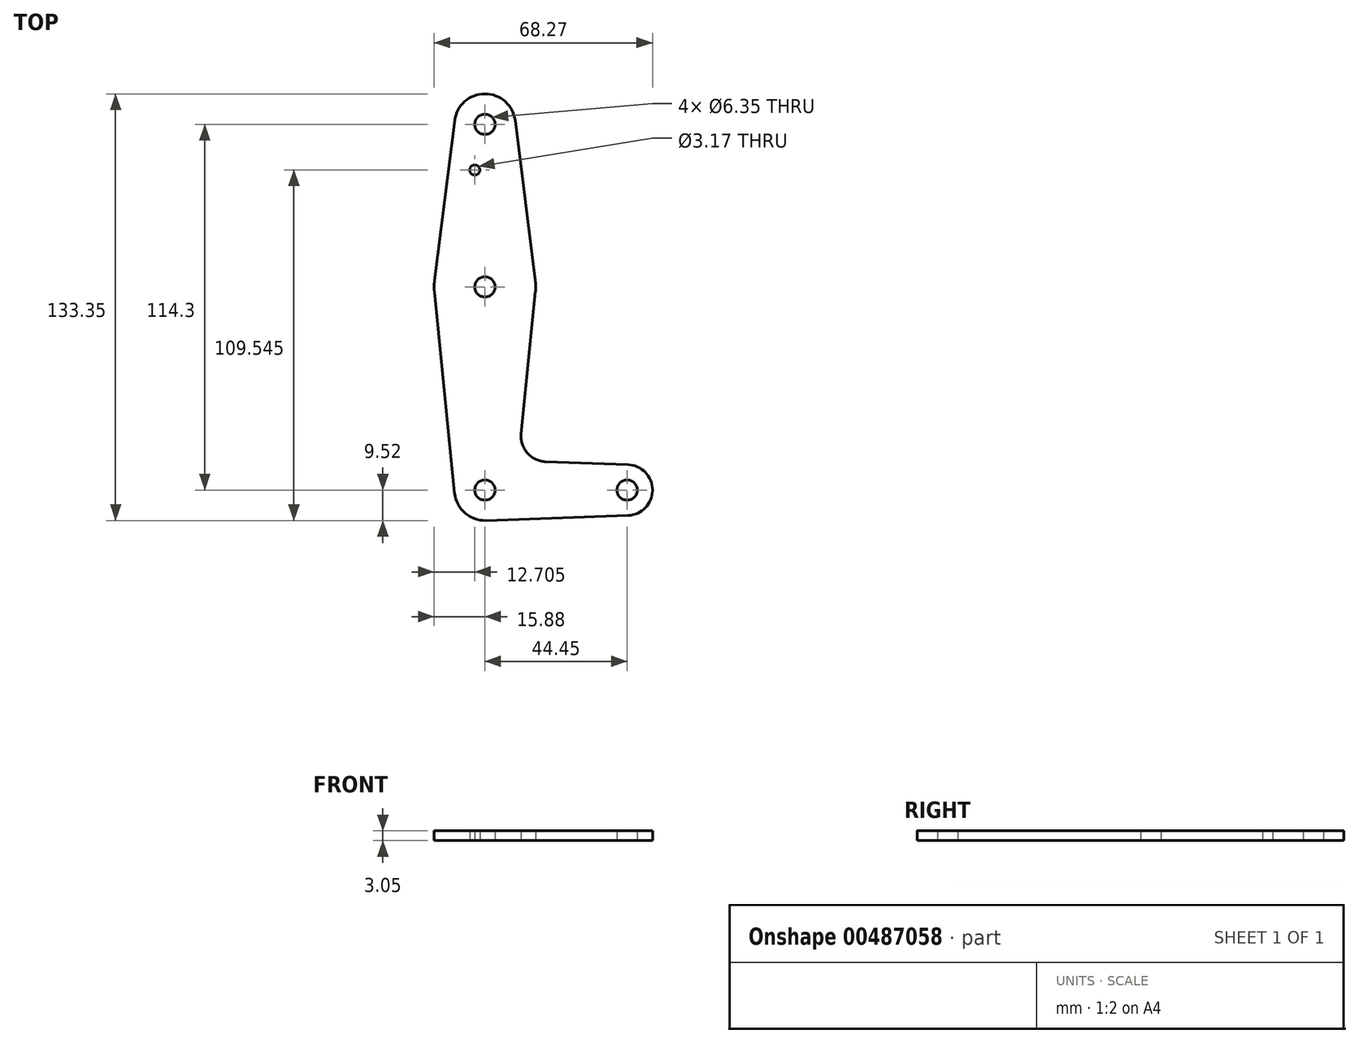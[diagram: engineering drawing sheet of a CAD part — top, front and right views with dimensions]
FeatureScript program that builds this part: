
annotation { "Feature Type Name" : "Feature", "Feature Type Description" : "" }
export const myFeature = defineFeature(function(context is Context, id is Id, definition is map)
    precondition{}
    {
        {
            var Q0;
            Q0=qCreatedBy(makeId("Top.planeOp"),FACE);
            var sketch = newSketch(context, id + "F0", { "sketchPlane" : qUnion([Q0])});
            skLineSegment(sketch, "E0", {"start": v(0, 0) * mm, "end": v(0, 114.3) * mm, "construction": true});
            skLineSegment(sketch, "E1", {"start": v(0, 0) * mm, "end": v(44.45, 0) * mm, "construction": true});
            skCircle(sketch, "E2", {"center": v(0, 0) * mm, "radius": 9.53 * mm});
            skCircle(sketch, "E3", {"center": v(0, 114.3) * mm, "radius": 9.53 * mm});
            skCircle(sketch, "E4", {"center": v(44.45, 0) * mm, "radius": 7.94 * mm});
            skCircle(sketch, "E5", {"center": v(0, 63.5) * mm, "radius": 15.88 * mm});
            skLineSegment(sketch, "E6", {"start": v(9.45, 115.5) * mm, "end": v(15.8, 65.13) * mm});
            skLineSegment(sketch, "E7", {"start": v(-15.8, 61.91) * mm, "end": v(-9.48, -0.95) * mm});
            skLineSegment(sketch, "E8", {"start": v(11.34, 17.6) * mm, "end": v(15.8, 61.91) * mm});
            skLineSegment(sketch, "E9", {"start": v(-9.45, 115.5) * mm, "end": v(-15.75, 65.48) * mm});
            skLineSegment(sketch, "E10", {"start": v(18.97, 8.85) * mm, "end": v(44.73, 7.93) * mm});
            skLineSegment(sketch, "E11", {"start": v(0.34, -9.52) * mm, "end": v(44.73, -7.93) * mm});
            skCircle(sketch, "E12", {"center": v(0, 114.3) * mm, "radius": 3.18 * mm});
            skCircle(sketch, "E13", {"center": v(-3.18, 100.03) * mm, "radius": 1.59 * mm});
            skCircle(sketch, "E14", {"center": v(0, 63.5) * mm, "radius": 3.18 * mm});
            skCircle(sketch, "E15", {"center": v(0, 0) * mm, "radius": 3.18 * mm});
            skCircle(sketch, "E16", {"center": v(44.45, 0) * mm, "radius": 3.18 * mm});
            skArc(sketch, "E17.filletArc", {"start": v(11.34, 17.6) * mm, "mid": v(13.26, 11.57) * mm, "end": v(18.97, 8.85) * mm});
            skSolve(sketch);
        }
        {
            var Q0;
            Q0=makeQuery(id+"F0.imprint","IMPRINT",FACE,{"disambiguationData":[TD([[makeQuery(id+"F0.imprint","IMPRINT",EDGE,{"derivedFrom":sQuery(id+"F0.wireOp",EDGE,"E12")}),-1.0]])]});
            var Q1;
            {var subQ5=sQuery(id+"F0.wireOp",EDGE,"E9");Q1=makeQuery(id+"F0.imprint","IMPRINT",FACE,{"disambiguationData":[TD([[makeQuery(id+"F0.imprint","IMPRINT",EDGE,{"derivedFrom":subQ5}),1.0]])]});}
            var Q2;
            Q2=makeQuery(id+"F0.imprint","IMPRINT",FACE,{"disambiguationData":[TD([[makeQuery(id+"F0.imprint","IMPRINT",EDGE,{"derivedFrom":sQuery(id+"F0.wireOp",EDGE,"E14")}),-1.0]])]});
            var Q3;
            Q3=makeQuery(id+"F0.imprint","IMPRINT",FACE,{"disambiguationData":[TD([[makeQuery(id+"F0.imprint","IMPRINT",EDGE,{"derivedFrom":sQuery(id+"F0.wireOp",EDGE,"E16")}),-1.0]])]});
            var Q4;
            Q4=makeQuery(id+"F0.imprint","IMPRINT",FACE,{"disambiguationData":[TD([[makeQuery(id+"F0.imprint","IMPRINT",EDGE,{"derivedFrom":sQuery(id+"F0.wireOp",EDGE,"E15")}),-1.0]])]});
            var Q5;
            {var subQ0=sQuery(id+"F0.wireOp",EDGE,"E7");Q5=makeQuery(id+"F0.imprint","IMPRINT",FACE,{"disambiguationData":[TD([[makeQuery(id+"F0.imprint","IMPRINT",EDGE,{"derivedFrom":subQ0}),1.0]])]});}
            extrude(context, id + "F1", {"entities" : qUnion([Q0, Q1, Q2, Q3, Q4, Q5]), "depth" : 3.05 * mm});
        }
    });
